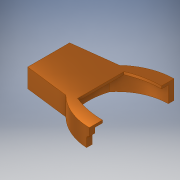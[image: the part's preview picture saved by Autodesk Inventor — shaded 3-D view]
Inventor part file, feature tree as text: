
AUTODESK INVENTOR PART (.ipt)
format: ipt  version: 2019 (Build 230136000, 136)  size: 1,509,888 bytes
history: native  units: mm
features: sketch x8, other x6, extrude x5, projected_geometry x5, plane x3, revolve x2, fillet x1
ambient origin geometry x8: Origin, YZ Plane, XZ Plane, XY Plane, X Axis, Y Axis, Z Axis, Center Point
bodies: Volumenkörper1 (feature_tree)
feature tree (30):
  sketch  "Skizze1"  dims[d9=15.2mm d12=13.036764mm]
  sketch  "Skizze2"  dims[d38=15.2mm d47=8.714705mm]
  sketch  "Skizze3"  dims[d49=8.715mm d57=15.197209mm]
  extrude  "Extrusion1"  Depth=13.036764mm
  extrude  "Extrusion3"  Depth=8.714705mm
  extrude  "Extrusion4"  Depth=15.197209mm
  extrude  "Extrusion5"  Depth=15.197209mm
  plane  "Arbeitsebene4"
  other  "Trennen4"
  plane  "Arbeitsebene5"
  plane  "Arbeitsebene3"
  other  "Trennen3"
  fillet  "Rundung5"  Radius=1.077mm
  extrude  "Extrusion6"  Depth=3.1mm
  revolve  "Umdrehung2"
  revolve  "Umdrehung3"
  other  "Bild2"
  other  "Bild3"
  other  "Bild4"
  sketch  "Skizze8"  dims[d58=15.197209mm d59=11.912488mm d60=1.077mm]
  projected_geometry  "Projizierte Kontur4"
  sketch  "Skizze9"  dims[d61=3.1mm d62=0.0mm d67=8.853mm]
  projected_geometry  "Projizierte Kontur5"
  sketch  "Skizze10"  dims[d69=0.0mm]
  projected_geometry  "Projizierte Kontur6"
  projected_geometry  "Projizierte Kontur7"
  sketch  "Skizze12"  dims[d70=8.853mm]
  projected_geometry  "Projizierte Kontur8"
  sketch  "Skizze13"  dims[d73=0.5mm d74=0.0mm d75=0.6mm d76=90.0deg d77=1.55mm d78=0.5mm d79=0.0mm d80=5.0mm d82=8.798192mm d84=4.0mm d85=4.0mm d86=4.8mm d87=0.0mm d91=1.745329mm d92=1.0mm d95=2.3mm d96=0.0mm d98=-2.268928mm d102=1.0mm d103=1.745329mm d104=1.0mm d105=1.0mm d112=10.07mm d116=9.964mm]
  other  "Arbeitsachse4"
